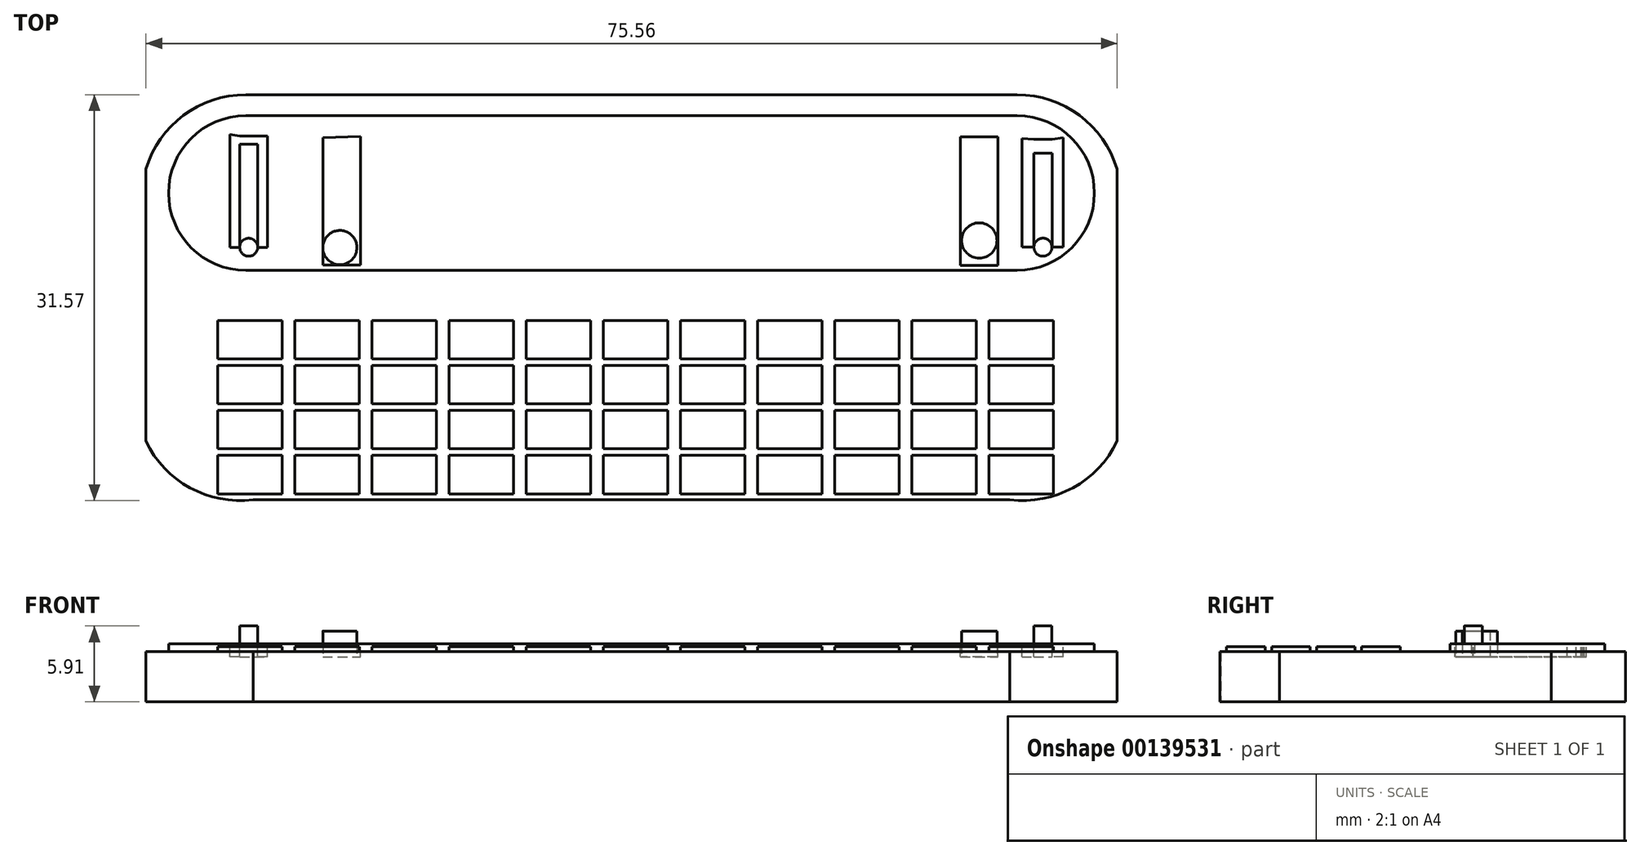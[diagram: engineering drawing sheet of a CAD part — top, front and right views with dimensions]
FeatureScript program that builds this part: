
annotation { "Feature Type Name" : "Feature", "Feature Type Description" : "" }
export const myFeature = defineFeature(function(context is Context, id is Id, definition is map)
    precondition{}
    {
        {
            var Q0;
            Q0=qCreatedBy(makeId("Top.planeOp"),FACE);
            var sketch = newSketch(context, id + "F0", { "sketchPlane" : qUnion([Q0])});
            skLineSegment(sketch, "E0.bottom", {"start": v(-50.5, 31.94) * mm, "end": v(9.5, 31.94) * mm});
            skLineSegment(sketch, "E0.top", {"start": v(-49.93, 0.43) * mm, "end": v(10.07, 0.43) * mm});
            skArc(sketch, "E1", {"start": v(-50.5, 31.94) * mm, "mid": v(-55.35, 30.33) * mm, "end": v(-58.27, 26.14) * mm});
            skArc(sketch, "E2", {"start": v(-58.27, 5) * mm, "mid": v(-54.84, 1.37) * mm, "end": v(-49.93, 0.43) * mm});
            skLineSegment(sketch, "E3", {"start": v(-58.27, 26.14) * mm, "end": v(-58.27, 5) * mm});
            skArc(sketch, "E4.MirrorCS", {"start": v(9.5, 31.94) * mm, "mid": v(14.36, 30.33) * mm, "end": v(17.3, 26.14) * mm});
            skArc(sketch, "E5.MirrorCS", {"start": v(17.3, 5) * mm, "mid": v(13.86, 1.37) * mm, "end": v(8.95, 0.43) * mm});
            skLineSegment(sketch, "E6", {"start": v(17.3, 26.14) * mm, "end": v(17.3, 5) * mm});
            skSolve(sketch);
        }
        {
            var Q0;
            Q0 = qSketchRegion(id + "F0", true);
            var Q1;
            Q1 = qConstructionFilter(qBodyType(qCreatedBy(id + "F0" ,EDGE), BodyType.WIRE), ConstructionObject.NO);
            extrude(context, id + "F1", {"entities" : qUnion([Q0]), "surfaceEntities" : qUnion([Q1]), "depth" : 3.9 * mm});
        }
        {
            var Q0;
            Q0=makeQuery(id+"F1.opExtrude","CAP_FACE",FACE,{"disambiguationData":[OSD([sQuery(id+"F0.wireOp",EDGE,"E0.bottom"),sQuery(id+"F0.wireOp",EDGE,"E0.top"),sQuery(id+"F0.wireOp",EDGE,"E1"),sQuery(id+"F0.wireOp",EDGE,"E2"),sQuery(id+"F0.wireOp",EDGE,"E3"),sQuery(id+"F0.wireOp",EDGE,"E4.MirrorCS"),sQuery(id+"F0.wireOp",EDGE,"E5.MirrorCS"),sQuery(id+"F0.wireOp",EDGE,"E6")])],"isStart":false});
            var sketch = newSketch(context, id + "F2", { "sketchPlane" : qUnion([Q0])});
            skLineSegment(sketch, "E7.bottom", {"start": v(-47.67, 11.39) * mm, "end": v(-52.67, 11.39) * mm});
            skLineSegment(sketch, "E7.top", {"start": v(-47.67, 14.39) * mm, "end": v(-52.67, 14.39) * mm});
            skLineSegment(sketch, "E7.left", {"start": v(-47.67, 11.39) * mm, "end": v(-47.67, 14.39) * mm});
            skLineSegment(sketch, "E7.right", {"start": v(-52.67, 11.39) * mm, "end": v(-52.67, 14.39) * mm});
            skPoint(sketch, "E7.middle", {"position": v(-50.17, 12.89) * mm});
            skLineSegment(sketch, "E8.0.1.0", {"start": v(-47.67, 10.89) * mm, "end": v(-52.67, 10.89) * mm});
            skLineSegment(sketch, "E8.0.1.1", {"start": v(-52.67, 7.89) * mm, "end": v(-52.67, 10.89) * mm});
            skLineSegment(sketch, "E8.0.1.2", {"start": v(-47.67, 7.89) * mm, "end": v(-52.67, 7.89) * mm});
            skLineSegment(sketch, "E8.0.1.3", {"start": v(-47.67, 7.89) * mm, "end": v(-47.67, 10.89) * mm});
            skLineSegment(sketch, "E8.0.2.0", {"start": v(-47.67, 7.39) * mm, "end": v(-52.67, 7.39) * mm});
            skLineSegment(sketch, "E8.0.2.1", {"start": v(-52.67, 4.39) * mm, "end": v(-52.67, 7.39) * mm});
            skLineSegment(sketch, "E8.0.2.2", {"start": v(-47.67, 4.39) * mm, "end": v(-52.67, 4.39) * mm});
            skLineSegment(sketch, "E8.0.2.3", {"start": v(-47.67, 4.39) * mm, "end": v(-47.67, 7.39) * mm});
            skLineSegment(sketch, "E8.0.3.0", {"start": v(-47.67, 3.89) * mm, "end": v(-52.67, 3.89) * mm});
            skLineSegment(sketch, "E8.0.3.1", {"start": v(-52.67, 0.89) * mm, "end": v(-52.67, 3.89) * mm});
            skLineSegment(sketch, "E8.0.3.2", {"start": v(-47.67, 0.89) * mm, "end": v(-52.67, 0.89) * mm});
            skLineSegment(sketch, "E8.0.3.3", {"start": v(-47.67, 0.89) * mm, "end": v(-47.67, 3.89) * mm});
            skLineSegment(sketch, "E8.1.0.0", {"start": v(-41.67, 14.39) * mm, "end": v(-46.67, 14.39) * mm});
            skLineSegment(sketch, "E8.1.0.1", {"start": v(-46.67, 11.39) * mm, "end": v(-46.67, 14.39) * mm});
            skLineSegment(sketch, "E8.1.0.2", {"start": v(-41.67, 11.39) * mm, "end": v(-46.67, 11.39) * mm});
            skLineSegment(sketch, "E8.1.0.3", {"start": v(-41.67, 11.39) * mm, "end": v(-41.67, 14.39) * mm});
            skLineSegment(sketch, "E8.1.1.0", {"start": v(-41.67, 10.89) * mm, "end": v(-46.67, 10.89) * mm});
            skLineSegment(sketch, "E8.1.1.1", {"start": v(-46.67, 7.89) * mm, "end": v(-46.67, 10.89) * mm});
            skLineSegment(sketch, "E8.1.1.2", {"start": v(-41.67, 7.89) * mm, "end": v(-46.67, 7.89) * mm});
            skLineSegment(sketch, "E8.1.1.3", {"start": v(-41.67, 7.89) * mm, "end": v(-41.67, 10.89) * mm});
            skLineSegment(sketch, "E8.1.2.0", {"start": v(-41.67, 7.39) * mm, "end": v(-46.67, 7.39) * mm});
            skLineSegment(sketch, "E8.1.2.1", {"start": v(-46.67, 4.39) * mm, "end": v(-46.67, 7.39) * mm});
            skLineSegment(sketch, "E8.1.2.2", {"start": v(-41.67, 4.39) * mm, "end": v(-46.67, 4.39) * mm});
            skLineSegment(sketch, "E8.1.2.3", {"start": v(-41.67, 4.39) * mm, "end": v(-41.67, 7.39) * mm});
            skLineSegment(sketch, "E8.1.3.0", {"start": v(-41.67, 3.89) * mm, "end": v(-46.67, 3.89) * mm});
            skLineSegment(sketch, "E8.1.3.1", {"start": v(-46.67, 0.89) * mm, "end": v(-46.67, 3.89) * mm});
            skLineSegment(sketch, "E8.1.3.2", {"start": v(-41.67, 0.89) * mm, "end": v(-46.67, 0.89) * mm});
            skLineSegment(sketch, "E8.1.3.3", {"start": v(-41.67, 0.89) * mm, "end": v(-41.67, 3.89) * mm});
            skLineSegment(sketch, "E8.2.0.0", {"start": v(-35.67, 14.39) * mm, "end": v(-40.67, 14.39) * mm});
            skLineSegment(sketch, "E8.2.0.1", {"start": v(-40.67, 11.39) * mm, "end": v(-40.67, 14.39) * mm});
            skLineSegment(sketch, "E8.2.0.2", {"start": v(-35.67, 11.39) * mm, "end": v(-40.67, 11.39) * mm});
            skLineSegment(sketch, "E8.2.0.3", {"start": v(-35.67, 11.39) * mm, "end": v(-35.67, 14.39) * mm});
            skLineSegment(sketch, "E8.2.1.0", {"start": v(-35.67, 10.89) * mm, "end": v(-40.67, 10.89) * mm});
            skLineSegment(sketch, "E8.2.1.1", {"start": v(-40.67, 7.89) * mm, "end": v(-40.67, 10.89) * mm});
            skLineSegment(sketch, "E8.2.1.2", {"start": v(-35.67, 7.89) * mm, "end": v(-40.67, 7.89) * mm});
            skLineSegment(sketch, "E8.2.1.3", {"start": v(-35.67, 7.89) * mm, "end": v(-35.67, 10.89) * mm});
            skLineSegment(sketch, "E8.2.2.0", {"start": v(-35.67, 7.39) * mm, "end": v(-40.67, 7.39) * mm});
            skLineSegment(sketch, "E8.2.2.1", {"start": v(-40.67, 4.39) * mm, "end": v(-40.67, 7.39) * mm});
            skLineSegment(sketch, "E8.2.2.2", {"start": v(-35.67, 4.39) * mm, "end": v(-40.67, 4.39) * mm});
            skLineSegment(sketch, "E8.2.2.3", {"start": v(-35.67, 4.39) * mm, "end": v(-35.67, 7.39) * mm});
            skLineSegment(sketch, "E8.2.3.0", {"start": v(-35.67, 3.89) * mm, "end": v(-40.67, 3.89) * mm});
            skLineSegment(sketch, "E8.2.3.1", {"start": v(-40.67, 0.89) * mm, "end": v(-40.67, 3.89) * mm});
            skLineSegment(sketch, "E8.2.3.2", {"start": v(-35.67, 0.89) * mm, "end": v(-40.67, 0.89) * mm});
            skLineSegment(sketch, "E8.2.3.3", {"start": v(-35.67, 0.89) * mm, "end": v(-35.67, 3.89) * mm});
            skLineSegment(sketch, "E8.3.0.0", {"start": v(-29.67, 14.39) * mm, "end": v(-34.67, 14.39) * mm});
            skLineSegment(sketch, "E8.3.0.1", {"start": v(-34.67, 11.39) * mm, "end": v(-34.67, 14.39) * mm});
            skLineSegment(sketch, "E8.3.0.2", {"start": v(-29.67, 11.39) * mm, "end": v(-34.67, 11.39) * mm});
            skLineSegment(sketch, "E8.3.0.3", {"start": v(-29.67, 11.39) * mm, "end": v(-29.67, 14.39) * mm});
            skLineSegment(sketch, "E8.3.1.0", {"start": v(-29.67, 10.89) * mm, "end": v(-34.67, 10.89) * mm});
            skLineSegment(sketch, "E8.3.1.1", {"start": v(-34.67, 7.89) * mm, "end": v(-34.67, 10.89) * mm});
            skLineSegment(sketch, "E8.3.1.2", {"start": v(-29.67, 7.89) * mm, "end": v(-34.67, 7.89) * mm});
            skLineSegment(sketch, "E8.3.1.3", {"start": v(-29.67, 7.89) * mm, "end": v(-29.67, 10.89) * mm});
            skLineSegment(sketch, "E8.3.2.0", {"start": v(-29.67, 7.39) * mm, "end": v(-34.67, 7.39) * mm});
            skLineSegment(sketch, "E8.3.2.1", {"start": v(-34.67, 4.39) * mm, "end": v(-34.67, 7.39) * mm});
            skLineSegment(sketch, "E8.3.2.2", {"start": v(-29.67, 4.39) * mm, "end": v(-34.67, 4.39) * mm});
            skLineSegment(sketch, "E8.3.2.3", {"start": v(-29.67, 4.39) * mm, "end": v(-29.67, 7.39) * mm});
            skLineSegment(sketch, "E8.3.3.0", {"start": v(-29.67, 3.89) * mm, "end": v(-34.67, 3.89) * mm});
            skLineSegment(sketch, "E8.3.3.1", {"start": v(-34.67, 0.89) * mm, "end": v(-34.67, 3.89) * mm});
            skLineSegment(sketch, "E8.3.3.2", {"start": v(-29.67, 0.89) * mm, "end": v(-34.67, 0.89) * mm});
            skLineSegment(sketch, "E8.3.3.3", {"start": v(-29.67, 0.89) * mm, "end": v(-29.67, 3.89) * mm});
            skLineSegment(sketch, "E8.4.0.0", {"start": v(-23.67, 14.39) * mm, "end": v(-28.67, 14.39) * mm});
            skLineSegment(sketch, "E8.4.0.1", {"start": v(-28.67, 11.39) * mm, "end": v(-28.67, 14.39) * mm});
            skLineSegment(sketch, "E8.4.0.2", {"start": v(-23.67, 11.39) * mm, "end": v(-28.67, 11.39) * mm});
            skLineSegment(sketch, "E8.4.0.3", {"start": v(-23.67, 11.39) * mm, "end": v(-23.67, 14.39) * mm});
            skLineSegment(sketch, "E8.4.1.0", {"start": v(-23.67, 10.89) * mm, "end": v(-28.67, 10.89) * mm});
            skLineSegment(sketch, "E8.4.1.1", {"start": v(-28.67, 7.89) * mm, "end": v(-28.67, 10.89) * mm});
            skLineSegment(sketch, "E8.4.1.2", {"start": v(-23.67, 7.89) * mm, "end": v(-28.67, 7.89) * mm});
            skLineSegment(sketch, "E8.4.1.3", {"start": v(-23.67, 7.89) * mm, "end": v(-23.67, 10.89) * mm});
            skLineSegment(sketch, "E8.4.2.0", {"start": v(-23.67, 7.39) * mm, "end": v(-28.67, 7.39) * mm});
            skLineSegment(sketch, "E8.4.2.1", {"start": v(-28.67, 4.39) * mm, "end": v(-28.67, 7.39) * mm});
            skLineSegment(sketch, "E8.4.2.2", {"start": v(-23.67, 4.39) * mm, "end": v(-28.67, 4.39) * mm});
            skLineSegment(sketch, "E8.4.2.3", {"start": v(-23.67, 4.39) * mm, "end": v(-23.67, 7.39) * mm});
            skLineSegment(sketch, "E8.4.3.0", {"start": v(-23.67, 3.89) * mm, "end": v(-28.67, 3.89) * mm});
            skLineSegment(sketch, "E8.4.3.1", {"start": v(-28.67, 0.89) * mm, "end": v(-28.67, 3.89) * mm});
            skLineSegment(sketch, "E8.4.3.2", {"start": v(-23.67, 0.89) * mm, "end": v(-28.67, 0.89) * mm});
            skLineSegment(sketch, "E8.4.3.3", {"start": v(-23.67, 0.89) * mm, "end": v(-23.67, 3.89) * mm});
            skLineSegment(sketch, "E8.5.0.0", {"start": v(-17.67, 14.39) * mm, "end": v(-22.67, 14.39) * mm});
            skLineSegment(sketch, "E8.5.0.1", {"start": v(-22.67, 11.39) * mm, "end": v(-22.67, 14.39) * mm});
            skLineSegment(sketch, "E8.5.0.2", {"start": v(-17.67, 11.39) * mm, "end": v(-22.67, 11.39) * mm});
            skLineSegment(sketch, "E8.5.0.3", {"start": v(-17.67, 11.39) * mm, "end": v(-17.67, 14.39) * mm});
            skLineSegment(sketch, "E8.5.1.0", {"start": v(-17.67, 10.89) * mm, "end": v(-22.67, 10.89) * mm});
            skLineSegment(sketch, "E8.5.1.1", {"start": v(-22.67, 7.89) * mm, "end": v(-22.67, 10.89) * mm});
            skLineSegment(sketch, "E8.5.1.2", {"start": v(-17.67, 7.89) * mm, "end": v(-22.67, 7.89) * mm});
            skLineSegment(sketch, "E8.5.1.3", {"start": v(-17.67, 7.89) * mm, "end": v(-17.67, 10.89) * mm});
            skLineSegment(sketch, "E8.5.2.0", {"start": v(-17.67, 7.39) * mm, "end": v(-22.67, 7.39) * mm});
            skLineSegment(sketch, "E8.5.2.1", {"start": v(-22.67, 4.39) * mm, "end": v(-22.67, 7.39) * mm});
            skLineSegment(sketch, "E8.5.2.2", {"start": v(-17.67, 4.39) * mm, "end": v(-22.67, 4.39) * mm});
            skLineSegment(sketch, "E8.5.2.3", {"start": v(-17.67, 4.39) * mm, "end": v(-17.67, 7.39) * mm});
            skLineSegment(sketch, "E8.5.3.0", {"start": v(-17.67, 3.89) * mm, "end": v(-22.67, 3.89) * mm});
            skLineSegment(sketch, "E8.5.3.1", {"start": v(-22.67, 0.89) * mm, "end": v(-22.67, 3.89) * mm});
            skLineSegment(sketch, "E8.5.3.2", {"start": v(-17.67, 0.89) * mm, "end": v(-22.67, 0.89) * mm});
            skLineSegment(sketch, "E8.5.3.3", {"start": v(-17.67, 0.89) * mm, "end": v(-17.67, 3.89) * mm});
            skLineSegment(sketch, "E8.6.0.0", {"start": v(-11.67, 14.39) * mm, "end": v(-16.67, 14.39) * mm});
            skLineSegment(sketch, "E8.6.0.1", {"start": v(-16.67, 11.39) * mm, "end": v(-16.67, 14.39) * mm});
            skLineSegment(sketch, "E8.6.0.2", {"start": v(-11.67, 11.39) * mm, "end": v(-16.67, 11.39) * mm});
            skLineSegment(sketch, "E8.6.0.3", {"start": v(-11.67, 11.39) * mm, "end": v(-11.67, 14.39) * mm});
            skLineSegment(sketch, "E8.6.1.0", {"start": v(-11.67, 10.89) * mm, "end": v(-16.67, 10.89) * mm});
            skLineSegment(sketch, "E8.6.1.1", {"start": v(-16.67, 7.89) * mm, "end": v(-16.67, 10.89) * mm});
            skLineSegment(sketch, "E8.6.1.2", {"start": v(-11.67, 7.89) * mm, "end": v(-16.67, 7.89) * mm});
            skLineSegment(sketch, "E8.6.1.3", {"start": v(-11.67, 7.89) * mm, "end": v(-11.67, 10.89) * mm});
            skLineSegment(sketch, "E8.6.2.0", {"start": v(-11.67, 7.39) * mm, "end": v(-16.67, 7.39) * mm});
            skLineSegment(sketch, "E8.6.2.1", {"start": v(-16.67, 4.39) * mm, "end": v(-16.67, 7.39) * mm});
            skLineSegment(sketch, "E8.6.2.2", {"start": v(-11.67, 4.39) * mm, "end": v(-16.67, 4.39) * mm});
            skLineSegment(sketch, "E8.6.2.3", {"start": v(-11.67, 4.39) * mm, "end": v(-11.67, 7.39) * mm});
            skLineSegment(sketch, "E8.6.3.0", {"start": v(-11.67, 3.89) * mm, "end": v(-16.67, 3.89) * mm});
            skLineSegment(sketch, "E8.6.3.1", {"start": v(-16.67, 0.89) * mm, "end": v(-16.67, 3.89) * mm});
            skLineSegment(sketch, "E8.6.3.2", {"start": v(-11.67, 0.89) * mm, "end": v(-16.67, 0.89) * mm});
            skLineSegment(sketch, "E8.6.3.3", {"start": v(-11.67, 0.89) * mm, "end": v(-11.67, 3.89) * mm});
            skLineSegment(sketch, "E8.7.0.0", {"start": v(-5.67, 14.39) * mm, "end": v(-10.67, 14.39) * mm});
            skLineSegment(sketch, "E8.7.0.1", {"start": v(-10.67, 11.39) * mm, "end": v(-10.67, 14.39) * mm});
            skLineSegment(sketch, "E8.7.0.2", {"start": v(-5.67, 11.39) * mm, "end": v(-10.67, 11.39) * mm});
            skLineSegment(sketch, "E8.7.0.3", {"start": v(-5.67, 11.39) * mm, "end": v(-5.67, 14.39) * mm});
            skLineSegment(sketch, "E8.7.1.0", {"start": v(-5.67, 10.89) * mm, "end": v(-10.67, 10.89) * mm});
            skLineSegment(sketch, "E8.7.1.1", {"start": v(-10.67, 7.89) * mm, "end": v(-10.67, 10.89) * mm});
            skLineSegment(sketch, "E8.7.1.2", {"start": v(-5.67, 7.89) * mm, "end": v(-10.67, 7.89) * mm});
            skLineSegment(sketch, "E8.7.1.3", {"start": v(-5.67, 7.89) * mm, "end": v(-5.67, 10.89) * mm});
            skLineSegment(sketch, "E8.7.2.0", {"start": v(-5.67, 7.39) * mm, "end": v(-10.67, 7.39) * mm});
            skLineSegment(sketch, "E8.7.2.1", {"start": v(-10.67, 4.39) * mm, "end": v(-10.67, 7.39) * mm});
            skLineSegment(sketch, "E8.7.2.2", {"start": v(-5.67, 4.39) * mm, "end": v(-10.67, 4.39) * mm});
            skLineSegment(sketch, "E8.7.2.3", {"start": v(-5.67, 4.39) * mm, "end": v(-5.67, 7.39) * mm});
            skLineSegment(sketch, "E8.7.3.0", {"start": v(-5.67, 3.89) * mm, "end": v(-10.67, 3.89) * mm});
            skLineSegment(sketch, "E8.7.3.1", {"start": v(-10.67, 0.89) * mm, "end": v(-10.67, 3.89) * mm});
            skLineSegment(sketch, "E8.7.3.2", {"start": v(-5.67, 0.89) * mm, "end": v(-10.67, 0.89) * mm});
            skLineSegment(sketch, "E8.7.3.3", {"start": v(-5.67, 0.89) * mm, "end": v(-5.67, 3.89) * mm});
            skLineSegment(sketch, "E8.8.0.0", {"start": v(0.33, 14.39) * mm, "end": v(-4.67, 14.39) * mm});
            skLineSegment(sketch, "E8.8.0.1", {"start": v(-4.67, 11.39) * mm, "end": v(-4.67, 14.39) * mm});
            skLineSegment(sketch, "E8.8.0.2", {"start": v(0.33, 11.39) * mm, "end": v(-4.67, 11.39) * mm});
            skLineSegment(sketch, "E8.8.0.3", {"start": v(0.33, 11.39) * mm, "end": v(0.33, 14.39) * mm});
            skLineSegment(sketch, "E8.8.1.0", {"start": v(0.33, 10.89) * mm, "end": v(-4.67, 10.89) * mm});
            skLineSegment(sketch, "E8.8.1.1", {"start": v(-4.67, 7.89) * mm, "end": v(-4.67, 10.89) * mm});
            skLineSegment(sketch, "E8.8.1.2", {"start": v(0.33, 7.89) * mm, "end": v(-4.67, 7.89) * mm});
            skLineSegment(sketch, "E8.8.1.3", {"start": v(0.33, 7.89) * mm, "end": v(0.33, 10.89) * mm});
            skLineSegment(sketch, "E8.8.2.0", {"start": v(0.33, 7.39) * mm, "end": v(-4.67, 7.39) * mm});
            skLineSegment(sketch, "E8.8.2.1", {"start": v(-4.67, 4.39) * mm, "end": v(-4.67, 7.39) * mm});
            skLineSegment(sketch, "E8.8.2.2", {"start": v(0.33, 4.39) * mm, "end": v(-4.67, 4.39) * mm});
            skLineSegment(sketch, "E8.8.2.3", {"start": v(0.33, 4.39) * mm, "end": v(0.33, 7.39) * mm});
            skLineSegment(sketch, "E8.8.3.0", {"start": v(0.33, 3.89) * mm, "end": v(-4.67, 3.89) * mm});
            skLineSegment(sketch, "E8.8.3.1", {"start": v(-4.67, 0.89) * mm, "end": v(-4.67, 3.89) * mm});
            skLineSegment(sketch, "E8.8.3.2", {"start": v(0.33, 0.89) * mm, "end": v(-4.67, 0.89) * mm});
            skLineSegment(sketch, "E8.8.3.3", {"start": v(0.33, 0.89) * mm, "end": v(0.33, 3.89) * mm});
            skLineSegment(sketch, "E8.9.0.0", {"start": v(6.33, 14.39) * mm, "end": v(1.33, 14.39) * mm});
            skLineSegment(sketch, "E8.9.0.1", {"start": v(1.33, 11.39) * mm, "end": v(1.33, 14.39) * mm});
            skLineSegment(sketch, "E8.9.0.2", {"start": v(6.33, 11.39) * mm, "end": v(1.33, 11.39) * mm});
            skLineSegment(sketch, "E8.9.0.3", {"start": v(6.33, 11.39) * mm, "end": v(6.33, 14.39) * mm});
            skLineSegment(sketch, "E8.9.1.0", {"start": v(6.33, 10.89) * mm, "end": v(1.33, 10.89) * mm});
            skLineSegment(sketch, "E8.9.1.1", {"start": v(1.33, 7.89) * mm, "end": v(1.33, 10.89) * mm});
            skLineSegment(sketch, "E8.9.1.2", {"start": v(6.33, 7.89) * mm, "end": v(1.33, 7.89) * mm});
            skLineSegment(sketch, "E8.9.1.3", {"start": v(6.33, 7.89) * mm, "end": v(6.33, 10.89) * mm});
            skLineSegment(sketch, "E8.9.2.0", {"start": v(6.33, 7.39) * mm, "end": v(1.33, 7.39) * mm});
            skLineSegment(sketch, "E8.9.2.1", {"start": v(1.33, 4.39) * mm, "end": v(1.33, 7.39) * mm});
            skLineSegment(sketch, "E8.9.2.2", {"start": v(6.33, 4.39) * mm, "end": v(1.33, 4.39) * mm});
            skLineSegment(sketch, "E8.9.2.3", {"start": v(6.33, 4.39) * mm, "end": v(6.33, 7.39) * mm});
            skLineSegment(sketch, "E8.9.3.0", {"start": v(6.33, 3.89) * mm, "end": v(1.33, 3.89) * mm});
            skLineSegment(sketch, "E8.9.3.1", {"start": v(1.33, 0.89) * mm, "end": v(1.33, 3.89) * mm});
            skLineSegment(sketch, "E8.9.3.2", {"start": v(6.33, 0.89) * mm, "end": v(1.33, 0.89) * mm});
            skLineSegment(sketch, "E8.9.3.3", {"start": v(6.33, 0.89) * mm, "end": v(6.33, 3.89) * mm});
            skLineSegment(sketch, "E8.10.0.0", {"start": v(12.33, 14.39) * mm, "end": v(7.33, 14.39) * mm});
            skLineSegment(sketch, "E8.10.0.1", {"start": v(7.33, 11.39) * mm, "end": v(7.33, 14.39) * mm});
            skLineSegment(sketch, "E8.10.0.2", {"start": v(12.33, 11.39) * mm, "end": v(7.33, 11.39) * mm});
            skLineSegment(sketch, "E8.10.0.3", {"start": v(12.33, 11.39) * mm, "end": v(12.33, 14.39) * mm});
            skLineSegment(sketch, "E8.10.1.0", {"start": v(12.33, 10.89) * mm, "end": v(7.33, 10.89) * mm});
            skLineSegment(sketch, "E8.10.1.1", {"start": v(7.33, 7.89) * mm, "end": v(7.33, 10.89) * mm});
            skLineSegment(sketch, "E8.10.1.2", {"start": v(12.33, 7.89) * mm, "end": v(7.33, 7.89) * mm});
            skLineSegment(sketch, "E8.10.1.3", {"start": v(12.33, 7.89) * mm, "end": v(12.33, 10.89) * mm});
            skLineSegment(sketch, "E8.10.2.0", {"start": v(12.33, 7.39) * mm, "end": v(7.33, 7.39) * mm});
            skLineSegment(sketch, "E8.10.2.1", {"start": v(7.33, 4.39) * mm, "end": v(7.33, 7.39) * mm});
            skLineSegment(sketch, "E8.10.2.2", {"start": v(12.33, 4.39) * mm, "end": v(7.33, 4.39) * mm});
            skLineSegment(sketch, "E8.10.2.3", {"start": v(12.33, 4.39) * mm, "end": v(12.33, 7.39) * mm});
            skLineSegment(sketch, "E8.10.3.0", {"start": v(12.33, 3.89) * mm, "end": v(7.33, 3.89) * mm});
            skLineSegment(sketch, "E8.10.3.1", {"start": v(7.33, 0.89) * mm, "end": v(7.33, 3.89) * mm});
            skLineSegment(sketch, "E8.10.3.2", {"start": v(12.33, 0.89) * mm, "end": v(7.33, 0.89) * mm});
            skLineSegment(sketch, "E8.10.3.3", {"start": v(12.33, 0.89) * mm, "end": v(12.33, 3.89) * mm});
            skLineSegment(sketch, "E8.direction1", {"start": v(-52.67, 14.39) * mm, "end": v(-46.67, 14.39) * mm, "construction": true});
            skLineSegment(sketch, "E8.direction2", {"start": v(-52.67, 14.39) * mm, "end": v(-52.67, 10.89) * mm, "construction": true});
            skSolve(sketch);
        }
        {
            var Q0;
            Q0 = qSketchRegion(id + "F2", true);
            extrude(context, id + "F3", {"entities" : qUnion([Q0]), "operationType" : NewBodyOperationType.ADD, "depth" : 0.4 * mm});
        }
        {
            var Q0;
            Q0=makeQuery(id+"F1.opExtrude","CAP_FACE",FACE,{"disambiguationData":[OSD([sQuery(id+"F0.wireOp",EDGE,"E0.bottom"),sQuery(id+"F0.wireOp",EDGE,"E0.top"),sQuery(id+"F0.wireOp",EDGE,"E1"),sQuery(id+"F0.wireOp",EDGE,"E2"),sQuery(id+"F0.wireOp",EDGE,"E3"),sQuery(id+"F0.wireOp",EDGE,"E4.MirrorCS"),sQuery(id+"F0.wireOp",EDGE,"E5.MirrorCS"),sQuery(id+"F0.wireOp",EDGE,"E6")])],"isStart":false});
            var sketch = newSketch(context, id + "F4", { "sketchPlane" : qUnion([Q0])});
            skLineSegment(sketch, "E9", {"start": v(-50.5, 30.31) * mm, "end": v(9.5, 30.31) * mm});
            skLineSegment(sketch, "E10", {"start": v(-50.5, 18.28) * mm, "end": v(9.5, 18.28) * mm});
            skArc(sketch, "E11", {"start": v(-50.5, 30.31) * mm, "mid": v(-56.5, 24.3) * mm, "end": v(-50.5, 18.28) * mm});
            skArc(sketch, "E12", {"start": v(9.5, 18.28) * mm, "mid": v(15.53, 24.3) * mm, "end": v(9.5, 30.31) * mm});
            skSolve(sketch);
        }
        {
            var Q0;
            Q0=makeQuery(id+"F4.imprint","IMPRINT",FACE,{"disambiguationData":[TD([[makeQuery(id+"F4.imprint","IMPRINT",EDGE,{"derivedFrom":sQuery(id+"F4.wireOp",EDGE,"E9")}),-1.0]])]});
            extrude(context, id + "F5", {"entities" : qUnion([Q0]), "operationType" : NewBodyOperationType.ADD, "depth" : 0.6 * mm});
        }
        {
            var Q0;
            Q0=makeQuery(id+"F1.opExtrude","CAP_FACE",FACE,{"disambiguationData":[OSD([sQuery(id+"F0.wireOp",EDGE,"E0.bottom"),sQuery(id+"F0.wireOp",EDGE,"E0.top"),sQuery(id+"F0.wireOp",EDGE,"E1"),sQuery(id+"F0.wireOp",EDGE,"E2"),sQuery(id+"F0.wireOp",EDGE,"E3"),sQuery(id+"F0.wireOp",EDGE,"E4.MirrorCS"),sQuery(id+"F0.wireOp",EDGE,"E5.MirrorCS"),sQuery(id+"F0.wireOp",EDGE,"E6")])],"isStart":false});
            var sketch = newSketch(context, id + "F6", { "sketchPlane" : qUnion([Q0])});
            skCircle(sketch, "E13", {"center": v(-50.27, 20.08) * mm, "radius": 0.7 * mm});
            skCircle(sketch, "E14", {"center": v(11.52, 20.08) * mm, "radius": 0.7 * mm});
            skSolve(sketch);
        }
        {
            var Q0;
            Q0 = qSketchRegion(id + "F6", true);
            extrude(context, id + "F7", {"entities" : qUnion([Q0]), "operationType" : NewBodyOperationType.ADD, "depth" : 2 * mm});
        }
        {
            var Q0;
            Q0=makeQuery(id+"F5.opExtrude","CAP_FACE",FACE,{"disambiguationData":[OSD([sQuery(id+"F4.wireOp",EDGE,"E9"),sQuery(id+"F4.wireOp",EDGE,"E10"),sQuery(id+"F4.wireOp",EDGE,"E11"),sQuery(id+"F4.wireOp",EDGE,"E12")])],"isStart":false});
            var sketch = newSketch(context, id + "F8", { "sketchPlane" : qUnion([Q0])});
            skLineSegment(sketch, "E15", {"start": v(-44.5, 28.59) * mm, "end": v(-44.5, 18.7) * mm});
            skLineSegment(sketch, "E16", {"start": v(-44.5, 18.7) * mm, "end": v(-41.58, 18.7) * mm});
            skLineSegment(sketch, "E17", {"start": v(-41.58, 18.7) * mm, "end": v(-41.58, 28.7) * mm});
            skLineSegment(sketch, "E18", {"start": v(-41.58, 28.7) * mm, "end": v(-44.5, 28.59) * mm});
            skSolve(sketch);
        }
        {
            var Q0;
            Q0=makeQuery(id+"F8.imprint","IMPRINT",FACE,{"disambiguationData":[TD([[makeQuery(id+"F8.imprint","IMPRINT",EDGE,{"derivedFrom":sQuery(id+"F8.wireOp",EDGE,"E15")}),1.0]])]});
            extrude(context, id + "F9", {"entities" : qUnion([Q0]), "operationType" : NewBodyOperationType.REMOVE, "oppositeDirection" : true, "depth" : 1 * mm});
        }
        {
            var Q0;
            Q0=makeQuery(id+"F5.opExtrude","CAP_FACE",FACE,{"disambiguationData":[OSD([sQuery(id+"F4.wireOp",EDGE,"E9"),sQuery(id+"F4.wireOp",EDGE,"E10"),sQuery(id+"F4.wireOp",EDGE,"E11"),sQuery(id+"F4.wireOp",EDGE,"E12")])],"isStart":false});
            var sketch = newSketch(context, id + "F10", { "sketchPlane" : qUnion([Q0])});
            skLineSegment(sketch, "E19", {"start": v(8.03, 28.66) * mm, "end": v(8.03, 18.66) * mm});
            skLineSegment(sketch, "E20", {"start": v(8.03, 18.66) * mm, "end": v(5.1, 18.66) * mm});
            skLineSegment(sketch, "E21", {"start": v(5.1, 18.66) * mm, "end": v(5.1, 28.66) * mm});
            skLineSegment(sketch, "E22", {"start": v(5.1, 28.66) * mm, "end": v(8.03, 28.66) * mm});
            skSolve(sketch);
        }
        {
            var Q0;
            Q0=makeQuery(id+"F10.imprint","IMPRINT",FACE,{"disambiguationData":[TD([[makeQuery(id+"F10.imprint","IMPRINT",EDGE,{"derivedFrom":sQuery(id+"F10.wireOp",EDGE,"E19")}),-1.0]])]});
            extrude(context, id + "F11", {"entities" : qUnion([Q0]), "operationType" : NewBodyOperationType.REMOVE, "oppositeDirection" : true, "depth" : 1 * mm});
        }
        {
            var Q0;
            Q0=makeQuery(id+"F9.boolean.opBoolean","COPY",FACE,{"derivedFrom":makeQuery(id+"F9.opExtrude","CAP_FACE",FACE,{"disambiguationData":[OSD([sQuery(id+"F8.wireOp",EDGE,"E15"),sQuery(id+"F8.wireOp",EDGE,"E16"),sQuery(id+"F8.wireOp",EDGE,"E17"),sQuery(id+"F8.wireOp",EDGE,"E18")])],"isStart":false})});
            var sketch = newSketch(context, id + "F12", { "sketchPlane" : qUnion([Q0])});
            skCircle(sketch, "E23", {"center": v(-43.18, 20.05) * mm, "radius": 1.33 * mm});
            skSolve(sketch);
        }
        {
            var Q0;
            Q0 = qSketchRegion(id + "F12", true);
            extrude(context, id + "F13", {"entities" : qUnion([Q0]), "operationType" : NewBodyOperationType.ADD, "depth" : 2 * mm});
        }
        {
            var Q0;
            Q0=makeQuery(id+"F11.boolean.opBoolean","COPY",FACE,{"derivedFrom":makeQuery(id+"F11.opExtrude","CAP_FACE",FACE,{"disambiguationData":[OSD([sQuery(id+"F10.wireOp",EDGE,"E19"),sQuery(id+"F10.wireOp",EDGE,"E20"),sQuery(id+"F10.wireOp",EDGE,"E21"),sQuery(id+"F10.wireOp",EDGE,"E22")])],"isStart":false})});
            var sketch = newSketch(context, id + "F14", { "sketchPlane" : qUnion([Q0])});
            skCircle(sketch, "E24", {"center": v(6.57, 20.6) * mm, "radius": 1.38 * mm});
            skPoint(sketch, "E24.centerSnap0", {"position": v(6.57, 18.66) * mm});
            skSolve(sketch);
        }
        {
            var Q0;
            Q0 = qSketchRegion(id + "F14", true);
            extrude(context, id + "F15", {"entities" : qUnion([Q0]), "operationType" : NewBodyOperationType.ADD, "depth" : 2 * mm});
        }
        {
            var Q0;
            Q0=makeQuery(id+"F5.opExtrude","CAP_FACE",FACE,{"disambiguationData":[OSD([sQuery(id+"F4.wireOp",EDGE,"E9"),sQuery(id+"F4.wireOp",EDGE,"E10"),sQuery(id+"F4.wireOp",EDGE,"E11"),sQuery(id+"F4.wireOp",EDGE,"E12")])],"isStart":false});
            var sketch = newSketch(context, id + "F16", { "sketchPlane" : qUnion([Q0])});
            skLineSegment(sketch, "E25", {"start": v(-49.57, 20.05) * mm, "end": v(-49.57, 28.71) * mm});
            skLineSegment(sketch, "E26", {"start": v(-50.97, 20.05) * mm, "end": v(-50.97, 28.71) * mm});
            skLineSegment(sketch, "E27", {"start": v(-50.97, 28.71) * mm, "end": v(-49.57, 28.71) * mm});
            skLineSegment(sketch, "E28", {"start": v(-51.75, 20.05) * mm, "end": v(-50.97, 20.05) * mm});
            skLineSegment(sketch, "E29", {"start": v(-51.75, 28.87) * mm, "end": v(-51.75, 20.05) * mm});
            skLineSegment(sketch, "E30", {"start": v(-50.97, 28.71) * mm, "end": v(-51.75, 28.87) * mm});
            skLineSegment(sketch, "E31", {"start": v(-48.82, 20.05) * mm, "end": v(-49.57, 20.05) * mm});
            skLineSegment(sketch, "E32", {"start": v(-48.82, 20.05) * mm, "end": v(-48.82, 28.71) * mm});
            skLineSegment(sketch, "E33", {"start": v(-48.82, 28.71) * mm, "end": v(-49.57, 28.71) * mm});
            skLineSegment(sketch, "E34", {"start": v(-50.97, 28.09) * mm, "end": v(-49.57, 28.09) * mm});
            skSolve(sketch);
        }
        {
            var Q0;
            Q0 = qSketchRegion(id + "F16", true);
            extrude(context, id + "F17", {"entities" : qUnion([Q0]), "operationType" : NewBodyOperationType.REMOVE, "oppositeDirection" : true, "depth" : 1 * mm});
        }
        {
            var Q0;
            {var subQ0=sQuery(id+"F4.wireOp",EDGE,"E10");var subQ1=sQuery(id+"F4.wireOp",EDGE,"E12");var subQ2=sQuery(id+"F4.wireOp",EDGE,"E9");var subQ3=sQuery(id+"F4.wireOp",EDGE,"E11");Q0=makeQuery(id+"F17.boolean.opBoolean","SPLIT",FACE,{"disambiguationData":[TD([makeQuery(id+"F5.opExtrude","SWEPT_FACE",FACE,{"disambiguationData":[OSD([subQ2])]})])],"derivedFrom":makeQuery(id+"F5.opExtrude","CAP_FACE",FACE,{"disambiguationData":[OSD([subQ2,subQ0,subQ3,subQ1])],"isStart":false})});}
            var sketch = newSketch(context, id + "F18", { "sketchPlane" : qUnion([Q0])});
            skLineSegment(sketch, "E35", {"start": v(12.23, 20.1) * mm, "end": v(12.23, 28.48) * mm});
            skLineSegment(sketch, "E36", {"start": v(10.82, 20.1) * mm, "end": v(10.82, 28.48) * mm});
            skLineSegment(sketch, "E37", {"start": v(10.82, 28.48) * mm, "end": v(12.23, 28.48) * mm});
            skLineSegment(sketch, "E38", {"start": v(10.82, 20.1) * mm, "end": v(9.88, 20.1) * mm});
            skLineSegment(sketch, "E39", {"start": v(9.88, 20.1) * mm, "end": v(9.88, 28.54) * mm});
            skLineSegment(sketch, "E40", {"start": v(9.88, 28.54) * mm, "end": v(10.82, 28.48) * mm});
            skLineSegment(sketch, "E41", {"start": v(12.23, 20.1) * mm, "end": v(13.11, 20.1) * mm});
            skLineSegment(sketch, "E42", {"start": v(13.11, 20.1) * mm, "end": v(13.11, 28.6) * mm});
            skLineSegment(sketch, "E43", {"start": v(13.11, 28.6) * mm, "end": v(12.23, 28.48) * mm});
            skLineSegment(sketch, "E44", {"start": v(10.82, 27.38) * mm, "end": v(12.23, 27.38) * mm});
            skSolve(sketch);
        }
        {
            var Q0;
            Q0 = qSketchRegion(id + "F18", true);
            extrude(context, id + "F19", {"entities" : qUnion([Q0]), "operationType" : NewBodyOperationType.REMOVE, "oppositeDirection" : true, "depth" : 1 * mm});
        }
    });
